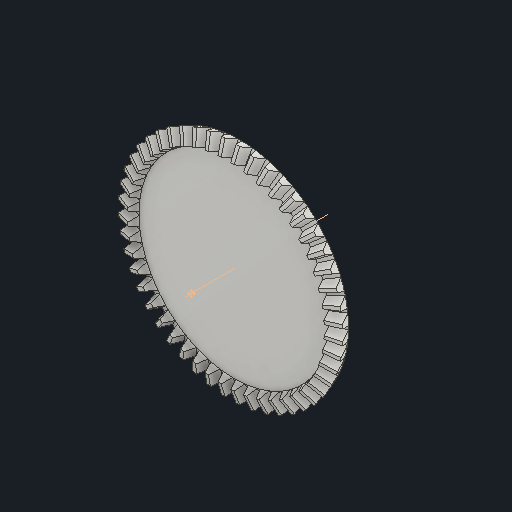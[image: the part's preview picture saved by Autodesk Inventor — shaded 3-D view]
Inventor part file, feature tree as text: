
AUTODESK INVENTOR PART (.ipt)
format: ipt  version: 2022 (Build 260153000, 153)  size: 709,120 bytes
history: native  units: mm
features: other x24, loft x2, pattern_circular x2, sketch x1
ambient origin geometry x6: Origin, XZ Plane, X Axis, Y Axis, Z Axis, Center Point
bodies: Solid1 (feature_tree)
feature tree (29):
  other  "Top Point"
  other  "Mesh Plane2"
  other  "Teeth Body"
  other  "Start Point"
  other  "Tooth Plane"
  other  "Start Sketch"
  other  "End Point"
  other  "3D Sketch Right"
  other  "End Plane Right"
  loft  "Loft Right"
  pattern_circular  "Circular Pattern Right"  [2 undecoded]
  other  "3D Sketch Left"
  other  "End Plane Left"
  loft  "Loft Left"
  pattern_circular  "Circular Pattern Left"  [2 undecoded]
  other  "Fix Body"
  other  "Mesh Plane"
  other  "Top Plane"
  other  "Teeth Body Sketch"
  other  "End Plane"
  other  "End Sketch"
  other  "Helical Curve Left"
  other  "End Sketch Left"
  other  "Body Sketch"
  sketch  "Sketch6"  dims[d0=120.0mm d1=118.488225mm d2=122.536758mm d3=8.0mm d4=20.545674mm d5=90.0deg d7=59.301777mm d8=57.411626mm d9=142.839828mm d11=8.275mm d12=51.697165mm d15=50.049398mm d16=124.522644mm d17=0.0mm d18=90.0deg d19=0.0mm d20=90.0deg d21=480.0mm d22=360.0deg d26=357.584802mm d27=3.045601mm d28=120.0mm d29=-11.938871mm d30=51.697165mm d31=50.049398mm d32=124.522644mm d35=0.0mm d37=0.0mm d39=0.0mm d40=90.0deg d41=480.0mm d42=360.0deg d46=90.0deg d47=90.0deg d48=0.0mm d49=0.0mm d50=90.0deg d51=0.654498mm d52=0.0mm d53=0.0mm d54=0.0mm d56=19.770163mm d57=168.118244mm d58=160.308244mm d59=146.559461mm d60=139.750983mm d61=146.559461mm d62=139.750983mm d65=357.584802mm d66=31.5mm d67=120.0mm d68=-11.938871mm d69=3.045601mm d70=50.049398mm d71=124.522644mm d72=51.697165mm d73=139.750983mm d74=146.559461mm d75=0.0mm d77=0.0mm d79=0.0mm d80=90.0deg d81=480.0mm d82=360.0deg d84=10.0mm d85=20.0mm d86=20.0mm d87=10.0mm d88=0.0mm d89=0.0mm d90=90.0deg d91=90.0deg d92=90.0deg d93=90.0deg]
  other  "Srf1"
  other  "Helical Curve Right"
  other  "End Sketch Right"
  other  "Pitch Diameter"
note: 4 required parameter values undecoded (feature->parameter linkage not recoverable at this tier; creation-order binding heuristic only, values carry confidence <= 0.55)
